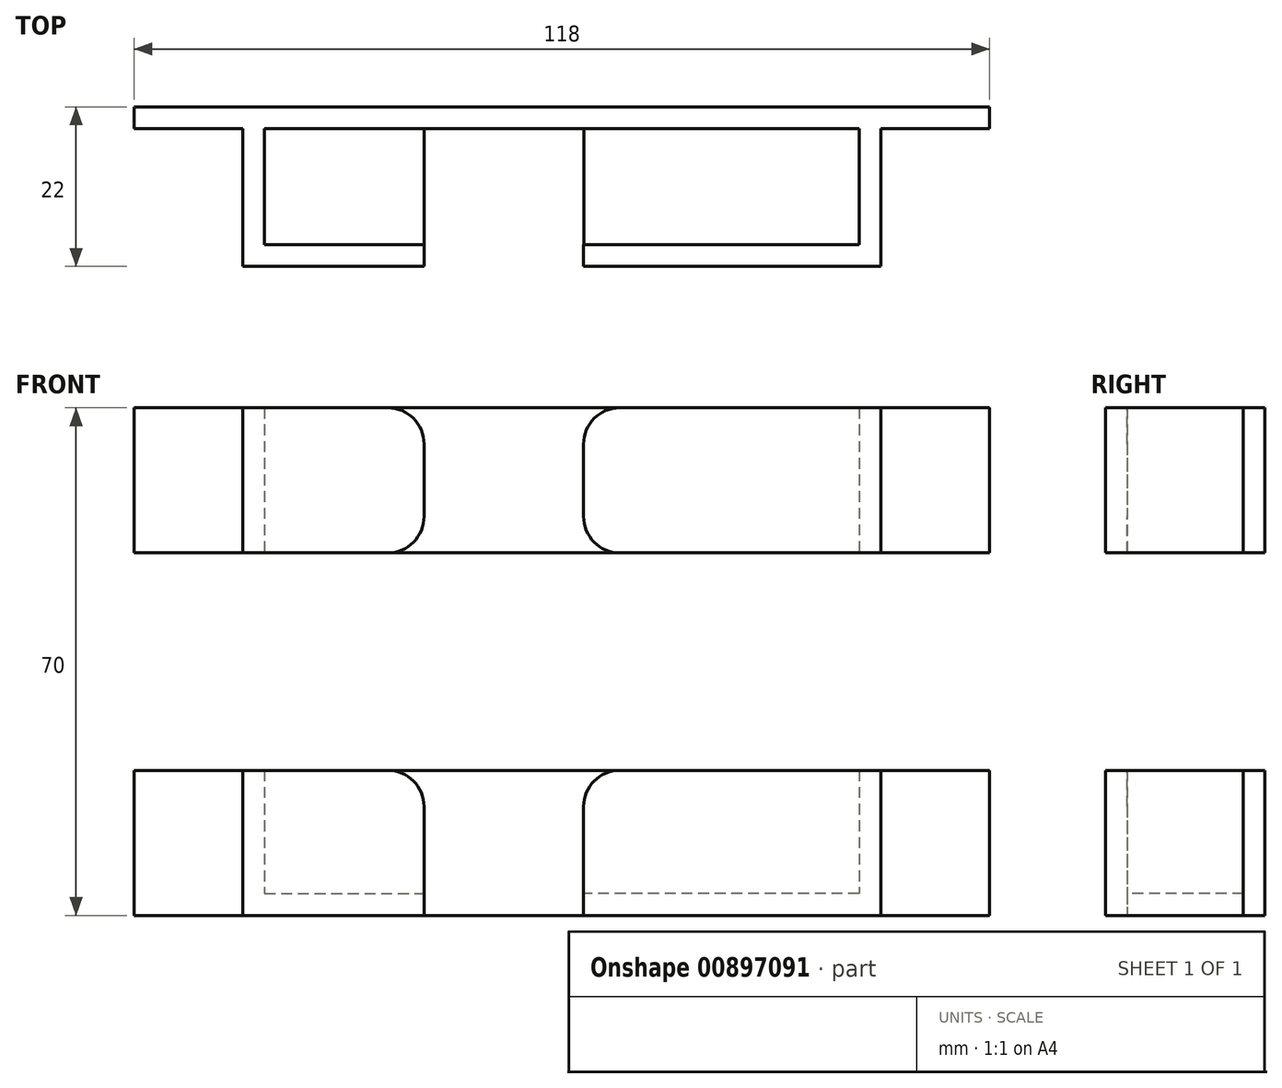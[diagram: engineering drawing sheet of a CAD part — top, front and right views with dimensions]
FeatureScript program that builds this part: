
annotation { "Feature Type Name" : "Feature", "Feature Type Description" : "" }
export const myFeature = defineFeature(function(context is Context, id is Id, definition is map)
    precondition{}
    {
        {
            var Q0;
            Q0=qCreatedBy(makeId("Top.planeOp"),FACE);
            var sketch = newSketch(context, id + "F0", { "sketchPlane" : qUnion([Q0])});
            skLineSegment(sketch, "E0.bottom", {"start": v(0, 0) * mm, "end": v(118, 0) * mm});
            skLineSegment(sketch, "E0.top", {"start": v(0, 3) * mm, "end": v(118, 3) * mm});
            skLineSegment(sketch, "E0.left", {"start": v(0, 0) * mm, "end": v(0, 3) * mm});
            skLineSegment(sketch, "E0.right", {"start": v(118, 0) * mm, "end": v(118, 3) * mm});
            skLineSegment(sketch, "E1", {"start": v(15, 0) * mm, "end": v(15, -19) * mm});
            skLineSegment(sketch, "E2", {"start": v(15, -19) * mm, "end": v(40, -19) * mm});
            skLineSegment(sketch, "E3", {"start": v(40, -19) * mm, "end": v(40, -16) * mm});
            skLineSegment(sketch, "E4", {"start": v(40, -16) * mm, "end": v(18, -16) * mm});
            skLineSegment(sketch, "E5", {"start": v(18, -16) * mm, "end": v(18, 0) * mm});
            skLineSegment(sketch, "E6", {"start": v(103, 0) * mm, "end": v(103, -19) * mm});
            skLineSegment(sketch, "E7", {"start": v(103, -19) * mm, "end": v(62, -19) * mm});
            skLineSegment(sketch, "E8", {"start": v(62, -19) * mm, "end": v(62, -16) * mm});
            skLineSegment(sketch, "E9", {"start": v(62, -16) * mm, "end": v(100, -16) * mm});
            skLineSegment(sketch, "E10", {"start": v(100, -16) * mm, "end": v(100, 0) * mm});
            skSolve(sketch);
        }
        {
            var Q0;
            Q0 = qSketchRegion(id + "F0", true);
            extrude(context, id + "F1", {"entities" : qUnion([Q0]), "depth" : 20 * mm, "offsetDistance" : 25 * mm});
        }
        {
            var Q0;
            Q0=makeQuery(id+"F1.opExtrude","CAP_FACE",FACE,{"disambiguationData":[OSD([sQuery(id+"F0.wireOp",EDGE,"E0.bottom"),sQuery(id+"F0.wireOp",EDGE,"E0.top"),sQuery(id+"F0.wireOp",EDGE,"E0.left"),sQuery(id+"F0.wireOp",EDGE,"E0.right"),sQuery(id+"F0.wireOp",EDGE,"E1"),sQuery(id+"F0.wireOp",EDGE,"E2"),sQuery(id+"F0.wireOp",EDGE,"E3"),sQuery(id+"F0.wireOp",EDGE,"E4"),sQuery(id+"F0.wireOp",EDGE,"E5"),sQuery(id+"F0.wireOp",EDGE,"E6"),sQuery(id+"F0.wireOp",EDGE,"E7"),sQuery(id+"F0.wireOp",EDGE,"E8"),sQuery(id+"F0.wireOp",EDGE,"E9"),sQuery(id+"F0.wireOp",EDGE,"E10")])],"isStart":true});
            cPlane(context, id + "F2", {"entities" : qUnion([Q0]), "cplaneType" : CPlaneType.OFFSET, "offset" : 0 * mm, "width" : 150 * mm, "height" : 150 * mm});
        }
        {
            var Q0;
            Q0=qCreatedBy(id+"F2.planeOp",FACE);
            var sketch = newSketch(context, id + "F3", { "sketchPlane" : qUnion([Q0])});
            skLineSegment(sketch, "E11.bottom", {"start": v(17.94, 16.05) * mm, "end": v(39.99, 16.05) * mm});
            skLineSegment(sketch, "E11.top", {"start": v(17.94, 0) * mm, "end": v(39.99, 0) * mm});
            skLineSegment(sketch, "E11.left", {"start": v(17.94, 16.05) * mm, "end": v(17.94, 0) * mm});
            skLineSegment(sketch, "E11.right", {"start": v(39.99, 16.05) * mm, "end": v(39.99, 0) * mm});
            skLineSegment(sketch, "E12.bottom", {"start": v(62.04, 16.46) * mm, "end": v(100.48, 16.46) * mm});
            skLineSegment(sketch, "E12.top", {"start": v(62.04, -0.89) * mm, "end": v(100.48, -0.89) * mm});
            skLineSegment(sketch, "E12.left", {"start": v(62.04, 16.46) * mm, "end": v(62.04, -0.89) * mm});
            skLineSegment(sketch, "E12.right", {"start": v(100.48, 16.46) * mm, "end": v(100.48, -0.89) * mm});
            skSolve(sketch);
        }
        {
            var Q0;
            Q0 = qSketchRegion(id + "F3", true);
            extrude(context, id + "F4", {"entities" : qUnion([Q0]), "operationType" : NewBodyOperationType.ADD, "oppositeDirection" : true, "depth" : 3 * mm, "offsetDistance" : 25 * mm});
        }
        {
            var Q0;
            Q0=makeQuery(id+"F1.opExtrude","CAP_EDGE",EDGE,{"disambiguationData":[OSD([sQuery(id+"F0.wireOp",EDGE,"E3")])],"isStart":false});
            var Q1;
            Q1=makeQuery(id+"F1.opExtrude","CAP_EDGE",EDGE,{"disambiguationData":[OSD([sQuery(id+"F0.wireOp",EDGE,"E8")])],"isStart":false});
            fillet(context, id + "F5", {"entities" : qUnion([Q0, Q1]), "radius" : 5 * mm, "tangentPropagation" : true, "allowEdgeOverflow" : false});
        }
        {
            var Q0;
            Q0=makeQuery(id+"F1.opExtrude","SWEPT_BODY",BODY,{"disambiguationData":[OSD([sQuery(id+"F0.wireOp",EDGE,"E0.bottom"),sQuery(id+"F0.wireOp",EDGE,"E0.top"),sQuery(id+"F0.wireOp",EDGE,"E0.left"),sQuery(id+"F0.wireOp",EDGE,"E0.right"),sQuery(id+"F0.wireOp",EDGE,"E1"),sQuery(id+"F0.wireOp",EDGE,"E2"),sQuery(id+"F0.wireOp",EDGE,"E3"),sQuery(id+"F0.wireOp",EDGE,"E4"),sQuery(id+"F0.wireOp",EDGE,"E5"),sQuery(id+"F0.wireOp",EDGE,"E6"),sQuery(id+"F0.wireOp",EDGE,"E7"),sQuery(id+"F0.wireOp",EDGE,"E8"),sQuery(id+"F0.wireOp",EDGE,"E9"),sQuery(id+"F0.wireOp",EDGE,"E10")])]});
            var Q1;
            Q1=makeQuery(id+"F1.opExtrude","SWEPT_EDGE",EDGE,{"disambiguationData":[OSD([sQuery(id+"F0.wireOp",EDGE,"E0.bottom"),sQuery(id+"F0.wireOp",EDGE,"E0.left")])]});
            transform(context, id + "F6", {"entities" : qUnion([Q0]), "transformType" : TransformType.TRANSLATION_DISTANCE, "transformDirection" : qUnion([Q1]), "distance" : 50 * mm, "oppositeDirection" : true, "makeCopy" : true});
        }
        {
            var Q0;
            Q0=makeQuery(id+"F6.opPattern","COPY",BODY,{"derivedFrom":makeQuery(id+"F1.opExtrude","SWEPT_BODY",BODY,{"disambiguationData":[OSD([sQuery(id+"F0.wireOp",EDGE,"E0.bottom"),sQuery(id+"F0.wireOp",EDGE,"E0.top"),sQuery(id+"F0.wireOp",EDGE,"E0.left"),sQuery(id+"F0.wireOp",EDGE,"E0.right"),sQuery(id+"F0.wireOp",EDGE,"E1"),sQuery(id+"F0.wireOp",EDGE,"E2"),sQuery(id+"F0.wireOp",EDGE,"E3"),sQuery(id+"F0.wireOp",EDGE,"E4"),sQuery(id+"F0.wireOp",EDGE,"E5"),sQuery(id+"F0.wireOp",EDGE,"E6"),sQuery(id+"F0.wireOp",EDGE,"E7"),sQuery(id+"F0.wireOp",EDGE,"E8"),sQuery(id+"F0.wireOp",EDGE,"E9"),sQuery(id+"F0.wireOp",EDGE,"E10")])]}),"instanceName":"1"});
            deleteBodies(context, id + "F7", {"entities" : qUnion([Q0])});
        }
        {
            var Q0;
            Q0=makeQuery(id+"F1.opExtrude","SWEPT_BODY",BODY,{"disambiguationData":[OSD([sQuery(id+"F0.wireOp",EDGE,"E0.bottom"),sQuery(id+"F0.wireOp",EDGE,"E0.top"),sQuery(id+"F0.wireOp",EDGE,"E0.left"),sQuery(id+"F0.wireOp",EDGE,"E0.right"),sQuery(id+"F0.wireOp",EDGE,"E1"),sQuery(id+"F0.wireOp",EDGE,"E2"),sQuery(id+"F0.wireOp",EDGE,"E3"),sQuery(id+"F0.wireOp",EDGE,"E4"),sQuery(id+"F0.wireOp",EDGE,"E5"),sQuery(id+"F0.wireOp",EDGE,"E6"),sQuery(id+"F0.wireOp",EDGE,"E7"),sQuery(id+"F0.wireOp",EDGE,"E8"),sQuery(id+"F0.wireOp",EDGE,"E9"),sQuery(id+"F0.wireOp",EDGE,"E10")])]});
            transform(context, id + "F8", {"entities" : qUnion([Q0]), "transformType" : TransformType.TRANSLATION_3D, "dx" : 0 * mm, "dy" : 0 * mm, "dz" : 50 * mm, "makeCopy" : true});
        }
        {
            var Q0;
            Q0=makeQuery(id+"F8.opPattern","COPY",FACE,{"derivedFrom":makeQuery(id+"F4.opExtrude","CAP_FACE",FACE,{"disambiguationData":[OSD([sQuery(id+"F3.wireOp",EDGE,"E11.bottom"),sQuery(id+"F3.wireOp",EDGE,"E11.top"),sQuery(id+"F3.wireOp",EDGE,"E11.left"),sQuery(id+"F3.wireOp",EDGE,"E11.right")])],"isStart":false}),"instanceName":"1"});
            extrude(context, id + "F9", {"entities" : qUnion([Q0]), "operationType" : NewBodyOperationType.REMOVE, "oppositeDirection" : true, "depth" : 25 * mm, "offsetDistance" : 25 * mm});
        }
        {
            var Q0;
            Q0=makeQuery(id+"F8.opPattern","COPY",FACE,{"derivedFrom":makeQuery(id+"F4.opExtrude","CAP_FACE",FACE,{"disambiguationData":[OSD([sQuery(id+"F3.wireOp",EDGE,"E12.bottom"),sQuery(id+"F3.wireOp",EDGE,"E12.top"),sQuery(id+"F3.wireOp",EDGE,"E12.left"),sQuery(id+"F3.wireOp",EDGE,"E12.right")])],"isStart":false}),"instanceName":"1"});
            extrude(context, id + "F10", {"entities" : qUnion([Q0]), "operationType" : NewBodyOperationType.REMOVE, "oppositeDirection" : true, "depth" : 3 * mm, "offsetDistance" : 25 * mm});
        }
        {
            var Q0;
            Q0=makeQuery(id+"F8.opPattern","COPY",EDGE,{"derivedFrom":makeQuery(id+"F1.opExtrude","CAP_EDGE",EDGE,{"disambiguationData":[OSD([sQuery(id+"F0.wireOp",EDGE,"E3")])],"isStart":true}),"instanceName":"1"});
            var Q1;
            Q1=makeQuery(id+"F8.opPattern","COPY",EDGE,{"derivedFrom":makeQuery(id+"F1.opExtrude","CAP_EDGE",EDGE,{"disambiguationData":[OSD([sQuery(id+"F0.wireOp",EDGE,"E8")])],"isStart":true}),"instanceName":"1"});
            fillet(context, id + "F11", {"entities" : qUnion([Q0, Q1]), "radius" : 5 * mm, "tangentPropagation" : true, "allowEdgeOverflow" : false});
        }
    });
